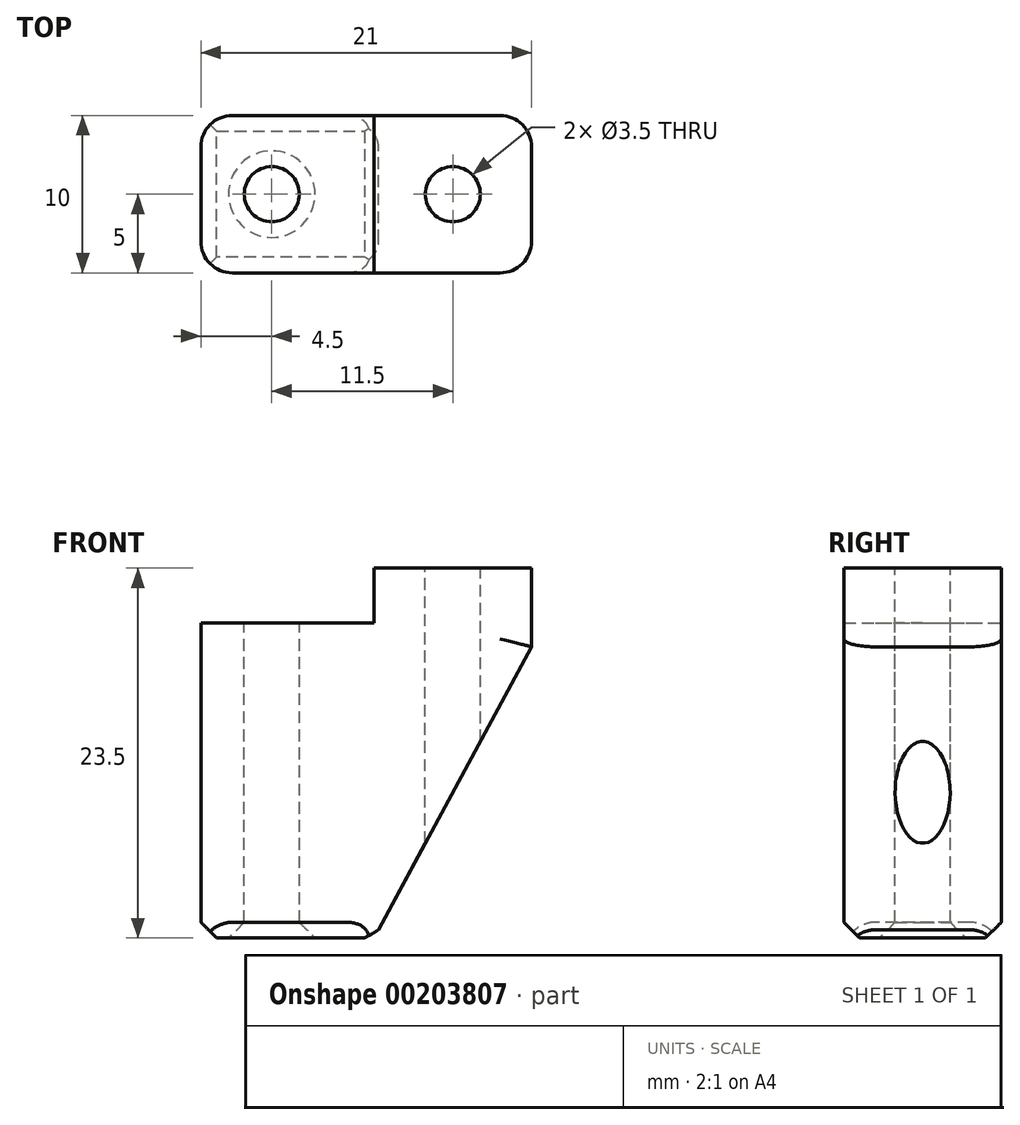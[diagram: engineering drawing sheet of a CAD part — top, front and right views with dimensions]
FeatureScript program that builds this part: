
annotation { "Feature Type Name" : "Feature", "Feature Type Description" : "" }
export const myFeature = defineFeature(function(context is Context, id is Id, definition is map)
    precondition{}
    {
        {
            var Q0;
            Q0=qCreatedBy(makeId("Front.planeOp"),FACE);
            var sketch = newSketch(context, id + "F0", { "sketchPlane" : qUnion([Q0])});
            skLineSegment(sketch, "E0", {"start": v(0, 0) * mm, "end": v(0, 3.5) * mm});
            skLineSegment(sketch, "E1", {"start": v(0, 3.5) * mm, "end": v(10, 3.5) * mm});
            skLineSegment(sketch, "E2", {"start": v(10, 3.5) * mm, "end": v(10, -1.5) * mm});
            skLineSegment(sketch, "E3", {"start": v(0, 0) * mm, "end": v(-11, 0) * mm});
            skLineSegment(sketch, "E4", {"start": v(-11, 0) * mm, "end": v(-11, -20) * mm});
            skLineSegment(sketch, "E5", {"start": v(-11, -20) * mm, "end": v(0, -20) * mm});
            skLineSegment(sketch, "E6", {"start": v(0, -20) * mm, "end": v(10, -1.5) * mm});
            skSolve(sketch);
        }
        {
            var Q0;
            Q0=makeQuery(id+"F0.imprint","IMPRINT",FACE,{"disambiguationData":[TD([[makeQuery(id+"F0.imprint","IMPRINT",EDGE,{"derivedFrom":sQuery(id+"F0.wireOp",EDGE,"E0")}),-1.0]])]});
            extrude(context, id + "F1", {"entities" : qUnion([Q0]), "depth" : 10 * mm, "symmetric" : true});
        }
        {
            var Q0;
            Q0=makeQuery(id+"F1.opExtrude","SWEPT_FACE",FACE,{"disambiguationData":[OSD([sQuery(id+"F0.wireOp",EDGE,"E1")])]});
            var sketch = newSketch(context, id + "F2", { "sketchPlane" : qUnion([Q0])});
            skLineSegment(sketch, "E7", {"start": v(0, 0) * mm, "end": v(5, 0) * mm, "construction": true});
            skPoint(sketch, "E7.endSnap0", {"position": v(0, 0) * mm});
            skLineSegment(sketch, "E8", {"start": v(0, 0) * mm, "end": v(-6.5, 0) * mm, "construction": true});
            skCircle(sketch, "E9", {"center": v(-6.5, 0) * mm, "radius": 1.75 * mm});
            skCircle(sketch, "E10", {"center": v(5, 0) * mm, "radius": 1.75 * mm});
            skSolve(sketch);
        }
        {
            var Q0;
            Q0=makeQuery(id+"F2.imprint","IMPRINT",FACE,{"disambiguationData":[TD([[makeQuery(id+"F2.imprint","IMPRINT",EDGE,{"derivedFrom":sQuery(id+"F2.wireOp",EDGE,"E9")}),1.0]])]});
            var Q1;
            Q1=makeQuery(id+"F2.imprint","IMPRINT",FACE,{"disambiguationData":[TD([[makeQuery(id+"F2.imprint","IMPRINT",EDGE,{"derivedFrom":sQuery(id+"F2.wireOp",EDGE,"E10")}),1.0]])]});
            extrude(context, id + "F3", {"entities" : qUnion([Q0, Q1]), "operationType" : NewBodyOperationType.REMOVE, "endBound" : BoundingType.THROUGH_ALL, "oppositeDirection" : true, "depth" : 25 * mm});
        }
        {
            var Q0;
            Q0=makeQuery(id+"F1.opExtrude","SWEPT_FACE",FACE,{"disambiguationData":[OSD([sQuery(id+"F0.wireOp",EDGE,"E5")])]});
            chamfer(context, id + "F4", {"entities" : qUnion([Q0]), "width" : 1 * mm, "tangentPropagation" : true});
        }
        {
            var Q0;
            Q0=makeQuery(id+"F1.opExtrude","CAP_EDGE",EDGE,{"disambiguationData":[OSD([sQuery(id+"F0.wireOp",EDGE,"E4")])],"isStart":false});
            var Q1;
            Q1=makeQuery(id+"F1.opExtrude","CAP_EDGE",EDGE,{"disambiguationData":[OSD([sQuery(id+"F0.wireOp",EDGE,"E4")])],"isStart":true});
            var Q2;
            Q2=makeQuery(id+"F1.opExtrude","CAP_EDGE",EDGE,{"disambiguationData":[OSD([sQuery(id+"F0.wireOp",EDGE,"E6")])],"isStart":false});
            var Q3;
            Q3=makeQuery(id+"F1.opExtrude","CAP_EDGE",EDGE,{"disambiguationData":[OSD([sQuery(id+"F0.wireOp",EDGE,"E2")])],"isStart":false});
            var Q4;
            Q4=makeQuery(id+"F1.opExtrude","CAP_EDGE",EDGE,{"disambiguationData":[OSD([sQuery(id+"F0.wireOp",EDGE,"E2")])],"isStart":true});
            var Q5;
            Q5=makeQuery(id+"F1.opExtrude","CAP_EDGE",EDGE,{"disambiguationData":[OSD([sQuery(id+"F0.wireOp",EDGE,"E6")])],"isStart":true});
            fillet(context, id + "F5", {"entities" : qUnion([Q0, Q1, Q2, Q3, Q4, Q5]), "radius" : 2 * mm, "tangentPropagation" : true, "allowEdgeOverflow" : false});
        }
    });
